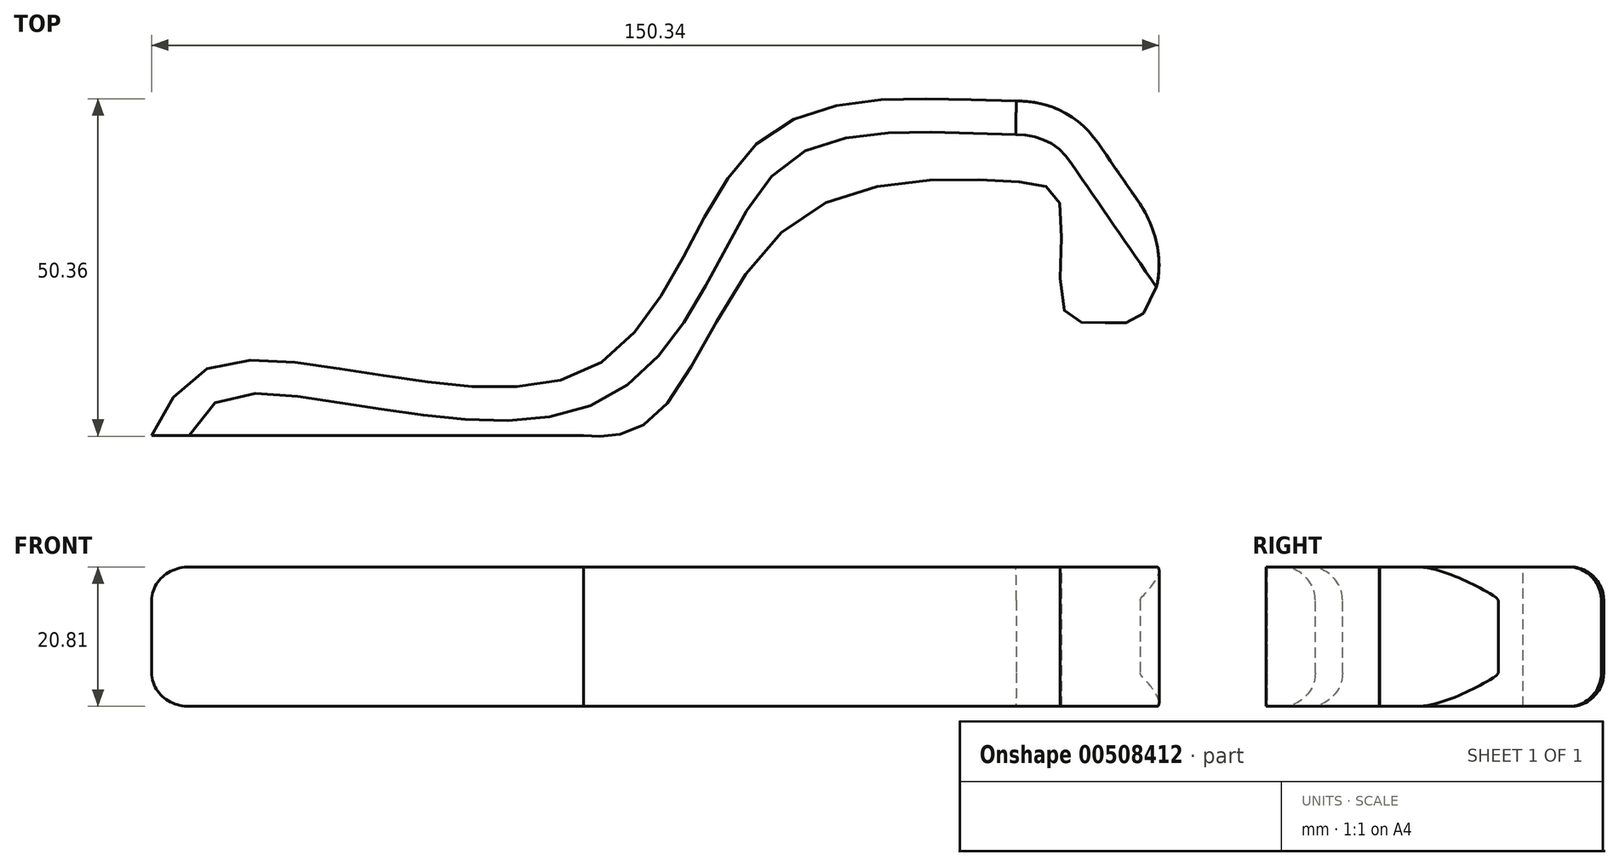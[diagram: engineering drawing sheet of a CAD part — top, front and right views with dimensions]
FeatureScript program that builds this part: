
annotation { "Feature Type Name" : "Feature", "Feature Type Description" : "" }
export const myFeature = defineFeature(function(context is Context, id is Id, definition is map)
    precondition{}
    {
        {
            var Q0;
            Q0=qCreatedBy(makeId("Top.planeOp"),FACE);
            var sketch = newSketch(context, id + "F0", { "sketchPlane" : qUnion([Q0])});
            skLineSegment(sketch, "E0", {"start": v(0, 0) * mm, "end": v(-64.47, 0) * mm});
            skFitSpline(sketch, "E1", {"points": [v(-64.47, 0) * mm, v(-52.86, 11) * mm, v(0, 9.47) * mm, v(25.97, 43.7) * mm, v(64.55, 49.93) * mm], "startDerivative": vector(44.37, 88.66) * mm, "endDerivative": vector(169.3, -3.4) * mm});
            skFitSpline(sketch, "E2", {"points": [v(64.55, 49.93) * mm, v(77.02, 43.3) * mm, v(83.02, 34.6) * mm], "startDerivative": vector(44.43, 0) * mm, "endDerivative": vector(38.78, -56.32) * mm});
            skFitSpline(sketch, "E3", {"points": [v(0, 0) * mm, v(3.97, 0) * mm, v(12.17, 4.45) * mm, v(32.28, 32.53) * mm, v(64.12, 37.93) * mm, v(70.99, 34.9) * mm, v(71.89, 18.35) * mm, v(77.9, 16.84) * mm, v(83.02, 17.76) * mm, v(83.02, 34.6) * mm], "startDerivative": vector(52.87, -1.44) * mm, "endDerivative": vector(-113.63, 177.54) * mm});
            skSolve(sketch);
        }
        {
            var Q0;
            Q0=makeQuery(id+"F0.imprint","IMPRINT",FACE,{"disambiguationData":[TD([[makeQuery(id+"F0.imprint","IMPRINT",EDGE,{"derivedFrom":sQuery(id+"F0.wireOp",EDGE,"E0")}),-1.0]])]});
            var Q1;
            Q1 = qSketchRegion(id + "FTqjy7GLTnjqft7_1", true);
            extrude(context, id + "F1", {"entities" : qUnion([Q0, Q1]), "depth" : 20.8 * mm});
        }
        {
            var Q0;
            Q0=makeQuery(id+"F1.opExtrude","CAP_EDGE",EDGE,{"disambiguationData":[OSD([sQuery(id+"F0.wireOp",EDGE,"E1")])],"isStart":false});
            var Q1;
            Q1=makeQuery(id+"F1.opExtrude","CAP_EDGE",EDGE,{"disambiguationData":[OSD([sQuery(id+"F0.wireOp",EDGE,"E1")])],"isStart":true});
            fillet(context, id + "F2", {"entities" : qUnion([Q0, Q1]), "radius" : 5 * mm, "tangentPropagation" : true, "allowEdgeOverflow" : false});
        }
    });
